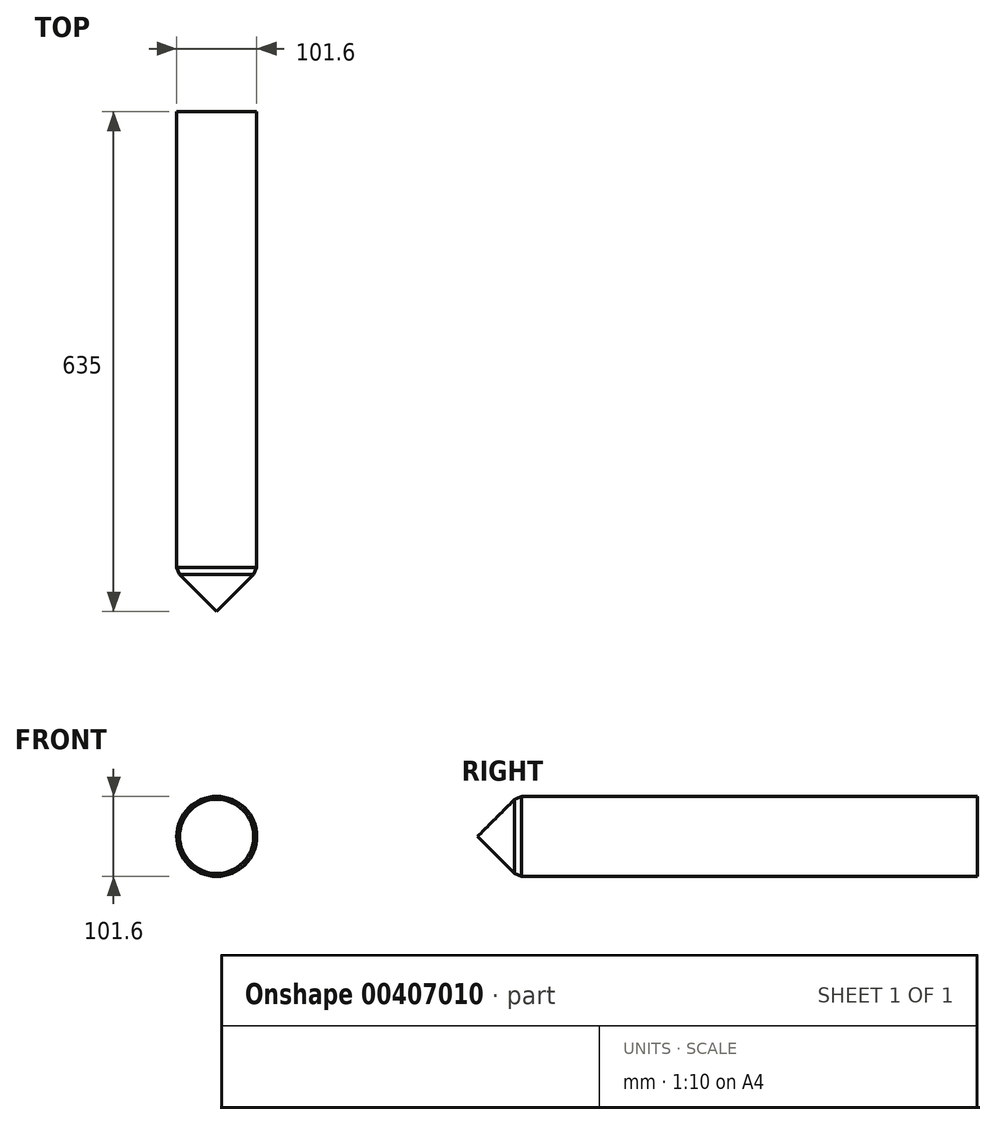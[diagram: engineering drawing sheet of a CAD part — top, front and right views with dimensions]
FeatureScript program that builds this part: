
annotation { "Feature Type Name" : "Feature", "Feature Type Description" : "" }
export const myFeature = defineFeature(function(context is Context, id is Id, definition is map)
    precondition{}
    {
        {
            var Q0;
            Q0=qCreatedBy(makeId("Front.planeOp"),FACE);
            var sketch = newSketch(context, id + "F0", { "sketchPlane" : qUnion([Q0])});
            skCircle(sketch, "E0", {"center": v(0, 0) * mm, "radius": 50.8 * mm});
            skSolve(sketch);
        }
        {
            var Q0;
            Q0=makeQuery(id+"F0.imprint","IMPRINT",FACE,{"disambiguationData":[TD([[makeQuery(id+"F0.imprint","IMPRINT",EDGE,{"derivedFrom":sQuery(id+"F0.wireOp",EDGE,"E0")}),1.0]])]});
            extrude(context, id + "F1", {"entities" : qUnion([Q0]), "endBound" : BoundingType.SYMMETRIC, "depth" : 635 * mm});
        }
        {
            var Q0;
            Q0=makeQuery(id+"F1.opExtrude","CAP_EDGE",EDGE,{"disambiguationData":[OSD([sQuery(id+"F0.wireOp",EDGE,"E0")])],"isStart":false});
            chamfer(context, id + "F2", {"entities" : qUnion([Q0]), "width" : 50.8 * mm, "tangentPropagation" : true});
        }
        {
            var Q0;
            {var subQ0=sQuery(id+"F0.wireOp",EDGE,"E0");Q0=makeQuery(id+"F2.opChamfer","BLEND_EDGE",EDGE,{"blendedFrom":[makeQuery(id+"F1.opExtrude","CAP_EDGE",EDGE,{"disambiguationData":[OSD([subQ0])],"isStart":false}),makeQuery(id+"F1.opExtrude","SWEPT_FACE",FACE,{"disambiguationData":[OSD([subQ0])]})],"blendedInto":[makeQuery(id+"F1.opExtrude","SWEPT_FACE",FACE,{"disambiguationData":[OSD([subQ0])]})]});}
            chamfer(context, id + "F3", {"entities" : qUnion([Q0]), "width" : 12.7 * mm, "tangentPropagation" : true});
        }
    });
